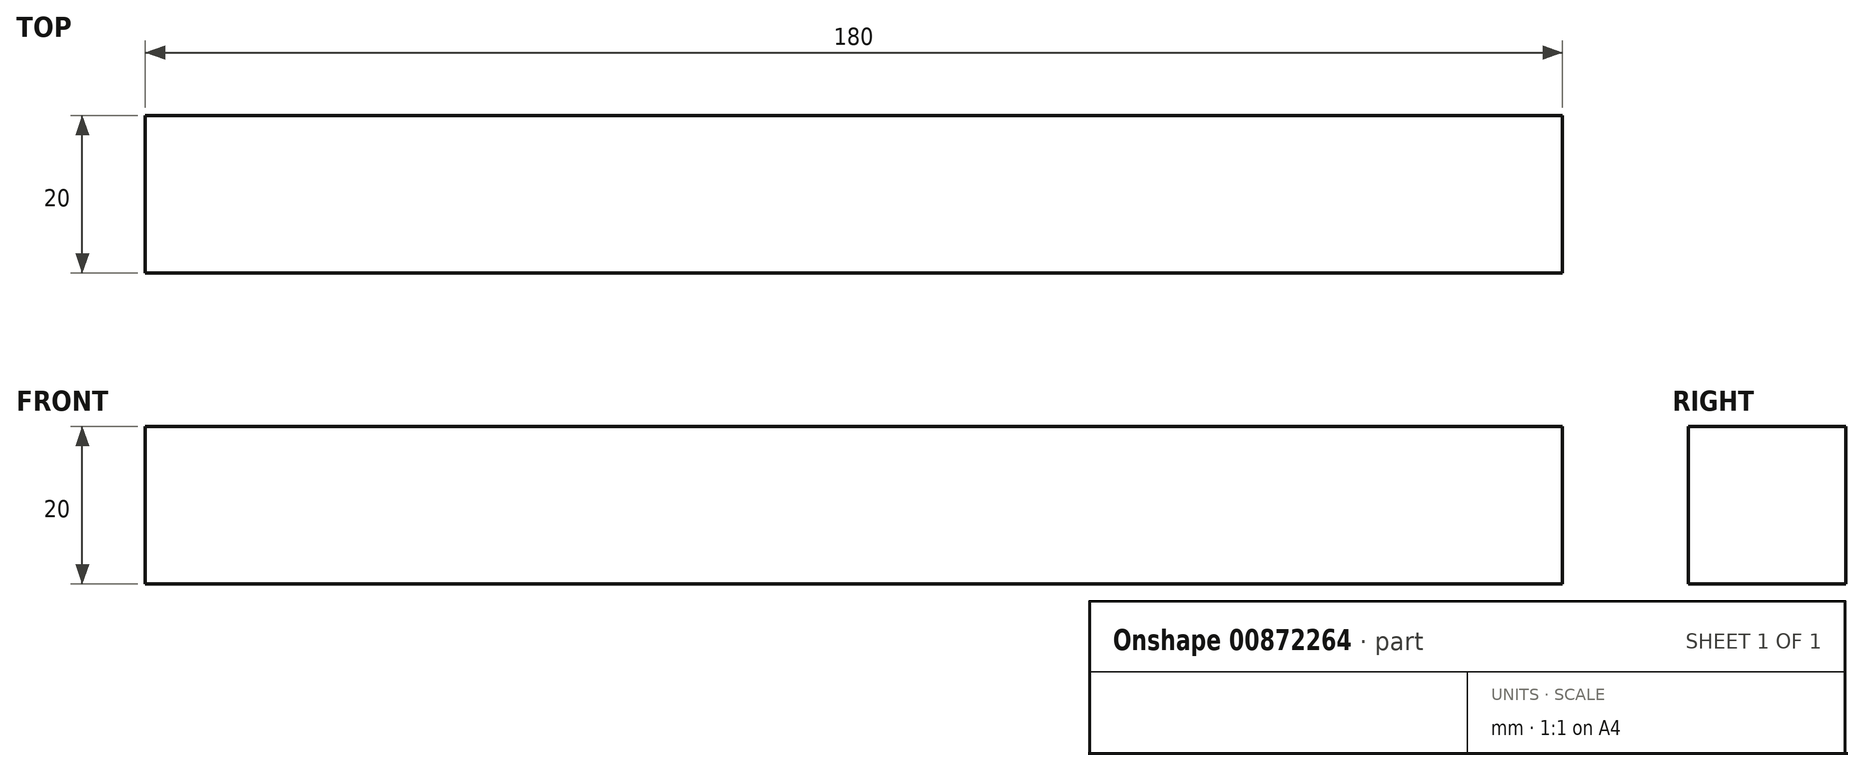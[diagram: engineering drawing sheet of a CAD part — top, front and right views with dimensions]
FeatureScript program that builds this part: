
annotation { "Feature Type Name" : "Feature", "Feature Type Description" : "" }
export const myFeature = defineFeature(function(context is Context, id is Id, definition is map)
    precondition{}
    {
        {
            var Q0;
            Q0=qCreatedBy(makeId("Front.planeOp"),FACE);
            var sketch = newSketch(context, id + "F0", { "sketchPlane" : qUnion([Q0])});
            skLineSegment(sketch, "E0.bottom", {"start": v(90, -10) * mm, "end": v(-90, -10) * mm});
            skLineSegment(sketch, "E0.top", {"start": v(90, 10) * mm, "end": v(-90, 10) * mm});
            skLineSegment(sketch, "E0.left", {"start": v(90, -10) * mm, "end": v(90, 10) * mm});
            skLineSegment(sketch, "E0.right", {"start": v(-90, -10) * mm, "end": v(-90, 10) * mm});
            skPoint(sketch, "E0.middle", {"position": v(0, 0) * mm});
            skSolve(sketch);
        }
        {
            var Q0;
            Q0=makeQuery(id+"F0.imprint","IMPRINT",FACE,{"disambiguationData":[TD([[makeQuery(id+"F0.imprint","IMPRINT",EDGE,{"derivedFrom":sQuery(id+"F0.wireOp",EDGE,"E0.bottom")}),-1.0]])]});
            extrude(context, id + "F1", {"entities" : qUnion([Q0]), "depth" : 20 * mm, "offsetDistance" : 25 * mm});
        }
    });
